# Revit family: 05-1798-14-14
name_source: partatom
category: Luminarias
revit_build: Autodesk Revit 2017 (Build: 20160225_1515(x64)
units: mm (PartAtom-declared; Revit-internal decimal feet)

## family parameters
Anfitrión = Cara
Compartido = Sí
Corte con vacíos al cargar = No
Cota de conector redondo = Diámetro de uso
Número OmniClass = 23.80.70.00
Origen de luz = No
Punto de cálculo de habitación = No
Tipo de pieza = Normal
Título OmniClass = Lighting

## types (1)
- 05-1798-14-14
    Acabado = Blanco
    CRI = 80
    Carga aparente = 0 VA
    Catálogo = Decorative
    CodigoGubimclass = 50.60.50.20
    CodigoOmniclass = 21-04 50 40
    CodigoUniclass2015 = EF_70_80
    CodigoUniformat2010 = D5040
    DescripcionGubimclass = Iluminación interior
    DescripcionOmniclass = Lighting
    DescripcionUniclass2015 = Lighting
    DescripcionUniformat2010 = Lighting
    EAN13 = 8435526800483
    Eficiencia energética = LED A++
    Elevación por defecto = 1000 mm  [stored 3.28084 ft]
    Etiqueta V/f = 100-240V/50-60Hz
    Fabricante = LEDS C4
    Familia = Ges Deco Rectangular 125mm
    FechaVersion = Julio 2020
    Ficha = http://files.leds-c4.com
    Fotometría = http://files.leds-c4.com
    Fuente de luz = 2xLED 4.4 330.00 lm
    IMC = http://files.leds-c4.com
    IP = IP20
    IfcExportAs = IfcLightFixture
IfcLightFixture
    IfcExportType = NOTDEFINED
    Imagen web = http://files.leds-c4.com
    LDT = http://files.leds-c4.com
    Lumenes reales (lm) = 93
    Material = Yeso
    Peso neto (KG) = 0.7
    Pluma comercial = http://files.leds-c4.com
    Producto descatalogado = Catalogado ES
    Rayo de luz = Check Photometric file
    Referencia = 05-1798-14-14
    Temperatura color led (K) = Blanco cálido - 3000K
    Tender text (Castellano) = LEDS C4
Ges Deco Rectangular 125mm
05-1798-14-14V2

Aplique de uso interior para iluminar hacia arriba y hacia abajo 

Ideal composiciones deco-tech. Diseño atemporal. Materiales naturales de alta calidad. Sin tornillos a la vista. Òptimo precio-rendimiento. Efecto de luz. Efecto de luz indirecto. Alta durabilidad para uso intensivo. Material estructura: Yeso. Acabado estructura: Blanco. Garantía: 5 Años.

Peso neto del producto (Kg): 0.700
Anchura o diámetro del producto (mm): 125
Altura del producto (mm): 125
Salida del producto (mm): 60

Clase 1. IP: IP20. LED. Nº de portalámparas o Leds: 2. Marca del LED: CREE. Marca del Driver: HEP. Potencia máxima de la fuente de luz: 4.4W. Temperatura de color: Blanco cálido - 3000K. Índice de reproducción cromática: 80. Steps Mac Adam: 3. Diámetro máximo de la bombilla que admite la luminaria: 50.000h L80B20. UGR: 44.5. Riesgo fotobiológico: RG2. Flujo real (lm): 93. Flujo nominal (lm): 330. Lm/W reales: 18. Voltaje: 3. Equipo incluido: Si, electrónico. Potencia total: 5.2. Factor de potencia: 0.50.
    Tender text (English) = LEDS C4
Ges Deco Rectangular 125mm
05-1798-14-14V2

Wall light for indoor use. 

For uplighting and downlighting. Ideal deco-tech compositions. Timeless design. High quality natural materials. No visible screws. Optimum price-performance. Light effect. Indirect light effect. High durability for intensive use. Structure material: Plaster. Structure finish: White. Warranty: 5 Years.

Product net weight (Kg): 0.700
Product width or diameter (mm): 125
Product height (mm): 125
Product aperture (mm): 60

Class 1. IP: IP20. LED. No. of lampholders or LEDs: 2. LED brand: CREE. Driver brand: HEP. Maximum power of light source: 4.4W. Colour temperature: LED warm-white 3000K. Colour rendering index: 80. MacAdam Steps: 3. Maximum diameter of luminaire bulb: 50.000h L80B20. UGR: 44.5. Photobiological risk: RG2. Real flux (lm): 93. Nominal flux (lm): 330. Lm/Real W: 18. Voltage: 3. Gear included: Yes, electronic. Total power: 5.2. Power factor: 0.50.
    Tipo = Aplique
    Vatios (W) = 5.2
    Versión = v1

note: [stored X ft] marks values corroborated as IEEE doubles in the binary element streams (Revit-internal decimal feet)
